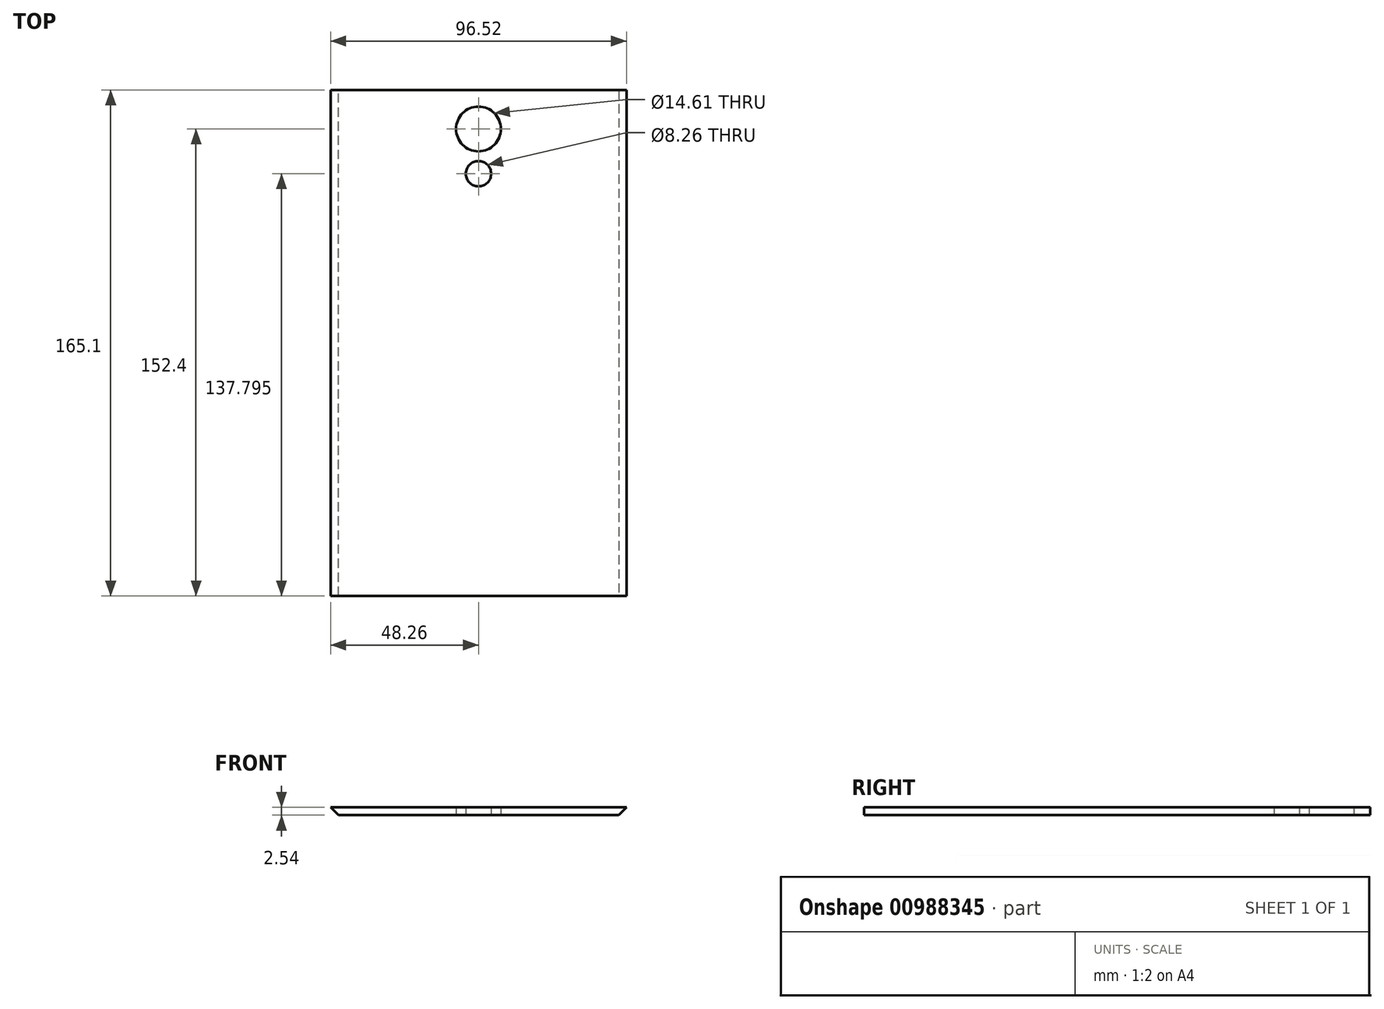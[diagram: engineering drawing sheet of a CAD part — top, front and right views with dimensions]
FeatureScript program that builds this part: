
annotation { "Feature Type Name" : "Feature", "Feature Type Description" : "" }
export const myFeature = defineFeature(function(context is Context, id is Id, definition is map)
    precondition{}
    {
        {
            var Q0;
            Q0=qCreatedBy(makeId("Top.planeOp"),FACE);
            var sketch = newSketch(context, id + "F0", { "sketchPlane" : qUnion([Q0])});
            skLineSegment(sketch, "E0.bottom", {"start": v(48.26, -82.55) * mm, "end": v(-48.26, -82.55) * mm});
            skLineSegment(sketch, "E0.top", {"start": v(48.26, 82.55) * mm, "end": v(-48.26, 82.55) * mm});
            skLineSegment(sketch, "E0.left", {"start": v(48.26, -82.55) * mm, "end": v(48.26, 82.55) * mm});
            skLineSegment(sketch, "E0.right", {"start": v(-48.26, -82.55) * mm, "end": v(-48.26, 82.55) * mm});
            skPoint(sketch, "E0.middle", {"position": v(0, 0) * mm});
            skCircle(sketch, "E1", {"center": v(0, 69.85) * mm, "radius": 7.3 * mm});
            skPoint(sketch, "E1.centerSnap0", {"position": v(0, 82.55) * mm});
            skCircle(sketch, "E2", {"center": v(0, 55.25) * mm, "radius": 4.13 * mm});
            skSolve(sketch);
        }
        {
            var Q0;
            Q0=makeQuery(id+"F0.imprint","IMPRINT",FACE,{"disambiguationData":[TD([[makeQuery(id+"F0.imprint","IMPRINT",EDGE,{"derivedFrom":sQuery(id+"F0.wireOp",EDGE,"E0.bottom")}),-1.0]])]});
            extrude(context, id + "F1", {"entities" : qUnion([Q0]), "depth" : 2.54 * mm, "offsetDistance" : 25.4 * mm});
        }
        {
            var Q0;
            Q0=makeQuery(id+"F1.opExtrude","CAP_EDGE",EDGE,{"disambiguationData":[OSD([sQuery(id+"F0.wireOp",EDGE,"E0.right")])],"isStart":true});
            var Q1;
            Q1=makeQuery(id+"F1.opExtrude","CAP_EDGE",EDGE,{"disambiguationData":[OSD([sQuery(id+"F0.wireOp",EDGE,"E0.left")])],"isStart":true});
            chamfer(context, id + "F2", {"entities" : qUnion([Q0, Q1]), "width" : 2.54 * mm, "tangentPropagation" : true});
        }
    });
